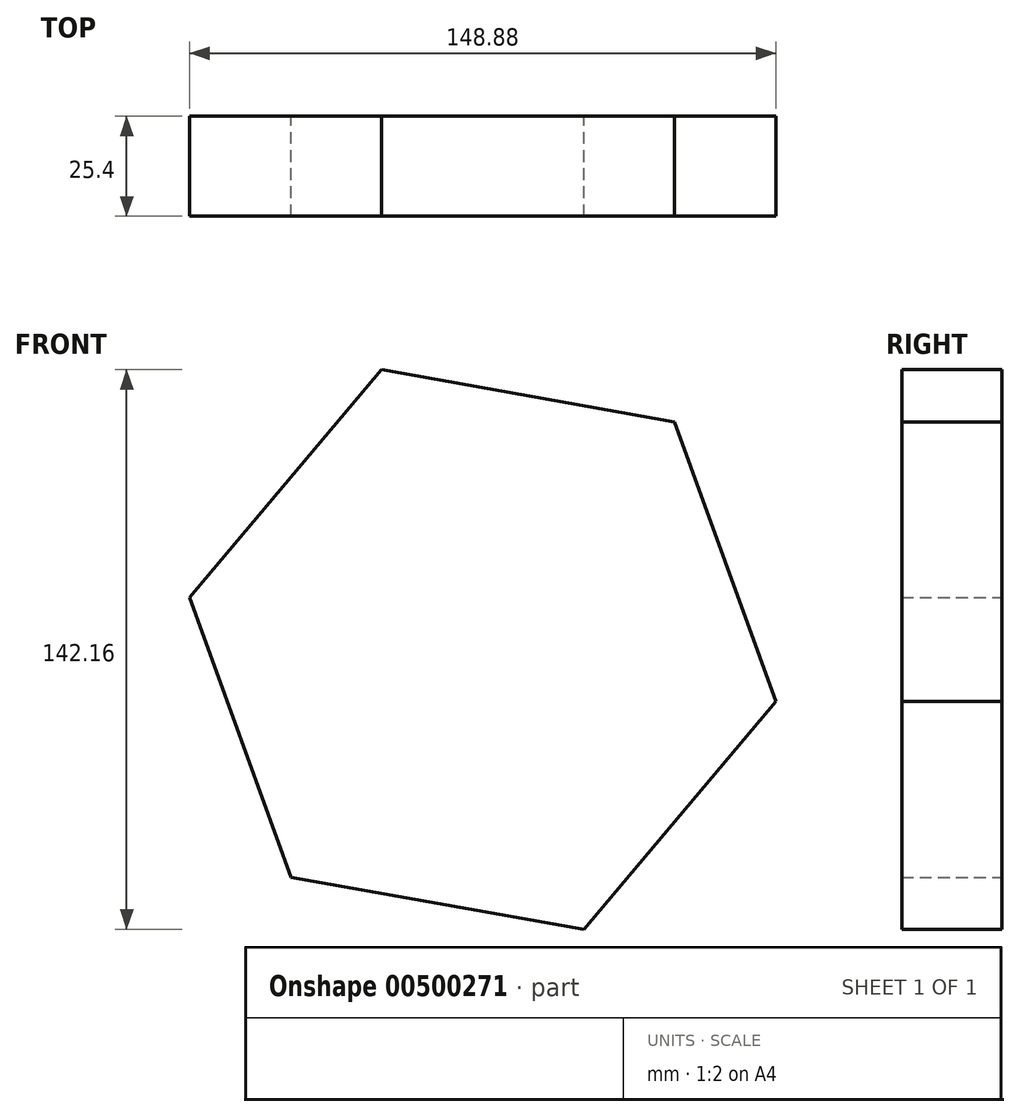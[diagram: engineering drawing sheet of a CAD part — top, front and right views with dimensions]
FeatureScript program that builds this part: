
annotation { "Feature Type Name" : "Feature", "Feature Type Description" : "" }
export const myFeature = defineFeature(function(context is Context, id is Id, definition is map)
    precondition{}
    {
        {
            var Q0;
            Q0=qCreatedBy(makeId("Front.planeOp"),FACE);
            var sketch = newSketch(context, id + "F0", { "sketchPlane" : qUnion([Q0])});
            skCircle(sketch, "E0.cCircle", {"center": v(0, 0) * mm, "radius": 75.61 * mm, "construction": true});
            skLineSegment(sketch, "E0.0", {"start": v(48.68, 57.86) * mm, "end": v(74.44, -13.23) * mm});
            skLineSegment(sketch, "E0.1", {"start": v(74.44, -13.23) * mm, "end": v(25.77, -71.08) * mm});
            skLineSegment(sketch, "E0.2", {"start": v(25.77, -71.08) * mm, "end": v(-48.68, -57.86) * mm});
            skLineSegment(sketch, "E0.3", {"start": v(-48.68, -57.86) * mm, "end": v(-74.44, 13.23) * mm});
            skLineSegment(sketch, "E0.4", {"start": v(-74.44, 13.23) * mm, "end": v(-25.77, 71.08) * mm});
            skLineSegment(sketch, "E0.5", {"start": v(-25.77, 71.08) * mm, "end": v(48.68, 57.86) * mm});
            skSolve(sketch);
        }
        {
            var Q0;
            Q0=makeQuery(id+"F0.imprint","IMPRINT",FACE,{"disambiguationData":[TD([[makeQuery(id+"F0.imprint","IMPRINT",EDGE,{"derivedFrom":sQuery(id+"F0.wireOp",EDGE,"E0.0")}),-1.0]])]});
            extrude(context, id + "F1", {"entities" : qUnion([Q0]), "depth" : 25.4 * mm});
        }
    });
